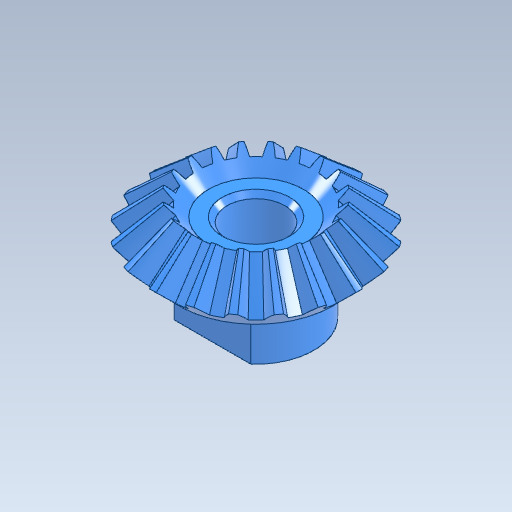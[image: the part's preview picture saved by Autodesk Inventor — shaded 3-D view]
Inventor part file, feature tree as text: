
AUTODESK INVENTOR PART (.ipt)
format: ipt  version: 2024 (Build 280153000, 153)  size: 437,248 bytes
history: native  units: mm
features: other x3, sketch x2, revolve x1, extrude x1
ambient origin geometry x8: Origin, YZ Plane, XZ Plane, XY Plane, X Axis, Y Axis, Z Axis, Center Point
bodies: Solid1 (feature_tree)
feature tree (7):
  other  "_PM1-20.ipt"
  sketch  "スケッチ1"
  sketch  "スケッチ2"
  revolve  "回転1"
  extrude  "押し出し1"  Depth=10.0mm
  other  "Solid1::_PM1-20.ipt"
  other  "TaggingFeature1"
